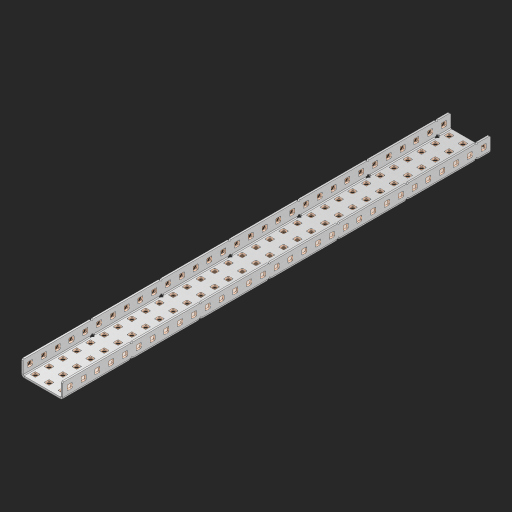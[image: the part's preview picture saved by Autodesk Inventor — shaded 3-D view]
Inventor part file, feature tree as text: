
AUTODESK INVENTOR PART (.ipt)
format: ipt  version: 2023 (Build 270158000, 158)  size: 1,850,368 bytes
history: native  units: in
note: dims shown in document units (in); Inventor stores cm internally (conversion verified against a paired STEP export)
features: other x160, extrude x154, sheet_metal_op x10, sketch x8, mirror x1, pattern_linear x1, chamfer x1
ambient origin geometry x8: Origin, YZ Plane, XZ Plane, XY Plane, X Axis, Y Axis, Z Axis, Center Point
bodies: Solid1 (feature_tree), Body (feature_tree)
feature tree (335):
  other  "Flange Pattern Plane"
  sheet_metal_op  "Flange Pattern"
  sheet_metal_op  "Body Pattern"
  other  "Arc Length"
  mirror  "Notch Mirror"
  pattern_linear  "Notch Pattern"  Spacing1=0.25in  [1 undecoded]
  chamfer  "End Chamfer"
  extrude  "Half Cut"  Depth=0.0625in
  sketch  "Sketch1"  dims[d0=1.5in]
  other  "Plate1"
  sketch  "Sketch2"  dims[d1=15.5in]
  other  "Plate2"
  sheet_metal_op  "Bend1"
  sheet_metal_op  "Corner1"
  sketch  "Sketch3"  dims[d2=0.0625in]
  other  "Flange Pattern Sketch"
  sketch  "Sketch7"  dims[d3=0.0625in]
  other  "Srf1"
  other  "Srf2"
  sketch  "Sketch8"  dims[d4=0.0312in]
  sketch  "Sketch9"  dims[d5=0.125in]
  other  "Srf91"
  sheet_metal_op  "Body Pattern Sketch"
  other  "Srf92"
  sketch  "Sketch13"  dims[d6=0.0625in]
  sketch  "Sketch14"  dims[d7=0.5in d8=90.0deg d9=0.0312in d10=0.25in d11=0.0625in d12=0.0625in d16=0.182in d17=0.02in d18=0.0625in d19=0.0in d20=0.25in d21=0.25in d46=0.172in d47=1.0in d48=0.0in d49=0.182in d50=0.02in d51=0.25in d52=0.25in d53=0.0625in d54=0.0in d55=0.172in d56=1.0in d57=0.0in d60=12.2047in d62=0.5in d63=1.1811in d65=0.5in d85=0.1473in d86=0.1782in d88=0.04in d89=0.0625in d90=0.0in d91=0.04in d92=0.0491in d95=2.5in d96=0.04in d97=0.25in d98=45.0deg d101=0.0in d102=2.497in d131=1.5in d132=12.2047in d134=0.5in d139=0.5in]
  other  "Srf856"
  other  "Srf1310"
  other  "Srf1311"
  other  "Srf1312"
  other  "Srf1376"
  other  "Srf1377"
  other  "Srf1728"
  other  "Srf1755"
  other  "Srf1878"
  other  "Srf1879"
  other  "Srf1880"
  other  "Srf1881"
  other  "Srf1882"
  other  "Srf1883"
  other  "Srf1884"
  other  "Srf1885"
  other  "Srf1886"
  other  "Srf1887"
  other  "Srf1888"
  other  "Srf1889"
  other  "Srf1890"
  other  "Srf1891"
  other  "Srf1892"
  other  "Srf1893"
  other  "Srf1894"
  other  "Srf1895"
  other  "Srf1896"
  other  "Srf1897"
  other  "Srf1898"
  other  "Srf1899"
  other  "Srf1900"
  other  "Srf1901"
  other  "Srf1902"
  other  "Srf1903"
  other  "Srf1904"
  other  "Srf1905"
  other  "Srf1906"
  other  "Srf1907"
  other  "Srf1908"
  other  "Srf1909"
  other  "Srf1910"
  other  "Srf1911"
  other  "Srf1912"
  other  "Srf1913"
  other  "Srf1914"
  other  "Srf1915"
  other  "Srf1916"
  other  "Srf1917"
  other  "Srf1918"
  other  "Srf1919"
  other  "Srf1920"
  other  "Srf1921"
  other  "Srf1922"
  other  "Srf1923"
  other  "Srf1924"
  other  "Srf1925"
  other  "Srf1926"
  other  "Srf1927"
  other  "Srf1928"
  other  "Srf1929"
  other  "Srf1930"
  other  "Srf1931"
  other  "Srf1932"
  other  "Srf1933"
  other  "Srf1942"
  other  "Srf1943"
  other  "Srf1944"
  other  "Srf1945"
  other  "Srf1946"
  other  "Srf1947"
  other  "Srf1948"
  other  "Srf1949"
  other  "Srf1950"
  other  "Srf1951"
  other  "Srf1952"
  other  "Srf1953"
  other  "Srf1954"
  other  "Srf1955"
  other  "Srf1956"
  other  "Srf1957"
  other  "Srf1958"
  other  "Srf1959"
  other  "Srf1960"
  other  "Srf1961"
  other  "Srf1962"
  other  "Srf1963"
  other  "Srf1964"
  other  "Srf1965"
  other  "Srf1966"
  other  "Srf1967"
  other  "Srf1968"
  other  "Srf1969"
  other  "Srf1970"
  other  "Srf1971"
  other  "Srf1972"
  other  "Srf1973"
  other  "Srf1974"
  other  "Srf1975"
  other  "Srf1976"
  other  "Srf1977"
  other  "Srf1978"
  other  "Srf1979"
  other  "Srf1980"
  other  "Srf1981"
  other  "Srf1982"
  other  "Srf1983"
  other  "Srf1984"
  other  "Srf1985"
  other  "Srf1986"
  other  "Srf1987"
  other  "Srf1988"
  other  "Srf1989"
  other  "Srf1990"
  other  "Srf1991"
  other  "Srf1992"
  other  "Srf1993"
  other  "Srf1994"
  other  "Srf1995"
  other  "Srf1996"
  other  "Srf1997"
  other  "Srf1998"
  other  "Srf1999"
  other  "Srf2000"
  other  "Srf2001"
  other  "Srf2002"
  other  "Srf2003"
  other  "Srf2004"
  other  "Srf2005"
  other  "Srf2006"
  other  "Srf2007"
  other  "Srf2008"
  other  "Srf2009"
  other  "Srf2010"
  other  "Srf2011"
  other  "Srf2012"
  other  "Srf2013"
  other  "Srf2014"
  other  "Srf2015"
  other  "Srf2016"
  other  "Srf2017"
  other  "Srf2018"
  other  "Srf2019"
  other  "Srf2020"
  other  "Srf2021"
  other  "Srf2022"
  other  "Srf2023"
  other  "Srf2024"
  other  "Srf2025"
  other  "Srf2026"
  other  "Srf2027"
  other  "Srf2028"
  sheet_metal_op  "Flange Stamp"
  sheet_metal_op  "Flange Circle"
  sheet_metal_op  "Body Stamp"
  sheet_metal_op  "Body Circle"
  sheet_metal_op  "Notch"
  extrude  "ExtrusionSrf2"  Depth=0.0625in
  extrude  "ExtrusionSrf92"  Depth=1.5in
  extrude  "ExtrusionSrf856"  Depth=0.02in
  extrude  "ExtrusionSrf1310"  Depth=0.0625in
  extrude  "ExtrusionSrf1311"  TaperAngle=0.0deg  [1 undecoded]
  extrude  "ExtrusionSrf1312"  Depth=0.25in
  extrude  "ExtrusionSrf1376"  Depth=0.25in
  extrude  "ExtrusionSrf1377"  Depth=1.5in
  extrude  "ExtrusionSrf1728"  Depth=1.5in TaperAngle=0.0deg
  extrude  "ExtrusionSrf1755"  Depth=1.5in
  extrude  "ExtrusionSrf1878"  Depth=0.02in
  extrude  "ExtrusionSrf1879"  Depth=0.25in
  extrude  "ExtrusionSrf1880"  Depth=0.25in
  extrude  "ExtrusionSrf1881"  Depth=0.0625in
  extrude  "ExtrusionSrf1882"  TaperAngle=0.0deg  [1 undecoded]
  extrude  "ExtrusionSrf1883"  Depth=1.5in
  extrude  "ExtrusionSrf1884"  Depth=1.5in TaperAngle=0.0deg
  extrude  "ExtrusionSrf1885"  Depth=1.5in
  extrude  "ExtrusionSrf1886"  Depth=1.5in
  extrude  "ExtrusionSrf1887"  Depth=1.5in
  extrude  "ExtrusionSrf1888"  Depth=1.5in
  extrude  "ExtrusionSrf1889"  Depth=1.5in
  extrude  "ExtrusionSrf1890"  Depth=0.0625in
  extrude  "ExtrusionSrf1891"  TaperAngle=0.0deg  [1 undecoded]
  extrude  "ExtrusionSrf1892"  Depth=1.5in
  extrude  "ExtrusionSrf1893"  Depth=1.5in
  extrude  "ExtrusionSrf1894"  Depth=1.5in
  extrude  "ExtrusionSrf1895"  Depth=0.25in TaperAngle=45.0deg
  extrude  "ExtrusionSrf1896"  TaperAngle=0.0deg  [1 undecoded]
  extrude  "ExtrusionSrf1897"  Depth=1.5in
  extrude  "ExtrusionSrf1898"  Depth=1.5in
  extrude  "ExtrusionSrf1899"  Depth=1.5in
  extrude  "ExtrusionSrf1900"  Depth=1.5in
  extrude  "ExtrusionSrf1901"  Depth=1.5in
  extrude  "ExtrusionSrf1902"  [1 undecoded]
  extrude  "ExtrusionSrf1903"  [1 undecoded]
  extrude  "ExtrusionSrf1904"  [1 undecoded]
  extrude  "ExtrusionSrf1905"  [1 undecoded]
  extrude  "ExtrusionSrf1906"  [1 undecoded]
  extrude  "ExtrusionSrf1907"  [1 undecoded]
  extrude  "ExtrusionSrf1908"  [1 undecoded]
  extrude  "ExtrusionSrf1909"  [1 undecoded]
  extrude  "ExtrusionSrf1910"  [1 undecoded]
  extrude  "ExtrusionSrf1911"  [1 undecoded]
  extrude  "ExtrusionSrf1912"  [1 undecoded]
  extrude  "ExtrusionSrf1913"  [1 undecoded]
  extrude  "ExtrusionSrf1914"  [1 undecoded]
  extrude  "ExtrusionSrf1915"  [1 undecoded]
  extrude  "ExtrusionSrf1916"  [1 undecoded]
  extrude  "ExtrusionSrf1917"  [1 undecoded]
  extrude  "ExtrusionSrf1918"  [1 undecoded]
  extrude  "ExtrusionSrf1919"  [1 undecoded]
  extrude  "ExtrusionSrf1920"  [1 undecoded]
  extrude  "ExtrusionSrf1921"  [1 undecoded]
  extrude  "ExtrusionSrf1922"  [1 undecoded]
  extrude  "ExtrusionSrf1923"  [1 undecoded]
  extrude  "ExtrusionSrf1924"  [1 undecoded]
  extrude  "ExtrusionSrf1925"  [1 undecoded]
  extrude  "ExtrusionSrf1926"  [1 undecoded]
  extrude  "ExtrusionSrf1927"  [1 undecoded]
  extrude  "ExtrusionSrf1928"  [1 undecoded]
  extrude  "ExtrusionSrf1929"  [1 undecoded]
  extrude  "ExtrusionSrf1930"  [1 undecoded]
  extrude  "ExtrusionSrf1931"  [1 undecoded]
  extrude  "ExtrusionSrf1932"  [1 undecoded]
  extrude  "ExtrusionSrf1933"  [1 undecoded]
  extrude  "ExtrusionSrf1942"  [1 undecoded]
  extrude  "ExtrusionSrf1943"  [1 undecoded]
  extrude  "ExtrusionSrf1944"  [1 undecoded]
  extrude  "ExtrusionSrf1945"  [1 undecoded]
  extrude  "ExtrusionSrf1946"  [1 undecoded]
  extrude  "ExtrusionSrf1947"  [1 undecoded]
  extrude  "ExtrusionSrf1948"  [1 undecoded]
  extrude  "ExtrusionSrf1949"  [1 undecoded]
  extrude  "ExtrusionSrf1950"  [1 undecoded]
  extrude  "ExtrusionSrf1951"  [1 undecoded]
  extrude  "ExtrusionSrf1952"  [1 undecoded]
  extrude  "ExtrusionSrf1953"  [1 undecoded]
  extrude  "ExtrusionSrf1954"  [1 undecoded]
  extrude  "ExtrusionSrf1955"  [1 undecoded]
  extrude  "ExtrusionSrf1956"  [1 undecoded]
  extrude  "ExtrusionSrf1957"  [1 undecoded]
  extrude  "ExtrusionSrf1958"  [1 undecoded]
  extrude  "ExtrusionSrf1959"  [1 undecoded]
  extrude  "ExtrusionSrf1960"  [1 undecoded]
  extrude  "ExtrusionSrf1961"  [1 undecoded]
  extrude  "ExtrusionSrf1962"  [1 undecoded]
  extrude  "ExtrusionSrf1963"  [1 undecoded]
  extrude  "ExtrusionSrf1964"  [1 undecoded]
  extrude  "ExtrusionSrf1965"  [1 undecoded]
  extrude  "ExtrusionSrf1966"  [1 undecoded]
  extrude  "ExtrusionSrf1967"  [1 undecoded]
  extrude  "ExtrusionSrf1968"  [1 undecoded]
  extrude  "ExtrusionSrf1969"  [1 undecoded]
  extrude  "ExtrusionSrf1970"  [1 undecoded]
  extrude  "ExtrusionSrf1971"  [1 undecoded]
  extrude  "ExtrusionSrf1972"  [1 undecoded]
  extrude  "ExtrusionSrf1973"  [1 undecoded]
  extrude  "ExtrusionSrf1974"  [1 undecoded]
  extrude  "ExtrusionSrf1975"  [1 undecoded]
  extrude  "ExtrusionSrf1976"  [1 undecoded]
  extrude  "ExtrusionSrf1977"  [1 undecoded]
  extrude  "ExtrusionSrf1978"  [1 undecoded]
  extrude  "ExtrusionSrf1979"  [1 undecoded]
  extrude  "ExtrusionSrf1980"  [1 undecoded]
  extrude  "ExtrusionSrf1981"  [1 undecoded]
  extrude  "ExtrusionSrf1982"  [1 undecoded]
  extrude  "ExtrusionSrf1983"  [1 undecoded]
  extrude  "ExtrusionSrf1984"  [1 undecoded]
  extrude  "ExtrusionSrf1985"  [1 undecoded]
  extrude  "ExtrusionSrf1986"  [1 undecoded]
  extrude  "ExtrusionSrf1987"  [1 undecoded]
  extrude  "ExtrusionSrf1988"  [1 undecoded]
  extrude  "ExtrusionSrf1989"  [1 undecoded]
  extrude  "ExtrusionSrf1990"  [1 undecoded]
  extrude  "ExtrusionSrf1991"  [1 undecoded]
  extrude  "ExtrusionSrf1992"  [1 undecoded]
  extrude  "ExtrusionSrf1993"  [1 undecoded]
  extrude  "ExtrusionSrf1994"  [1 undecoded]
  extrude  "ExtrusionSrf1995"  [1 undecoded]
  extrude  "ExtrusionSrf1996"  [1 undecoded]
  extrude  "ExtrusionSrf1997"  [1 undecoded]
  extrude  "ExtrusionSrf1998"  [1 undecoded]
  extrude  "ExtrusionSrf1999"  [1 undecoded]
  extrude  "ExtrusionSrf2000"  [1 undecoded]
  extrude  "ExtrusionSrf2001"  [1 undecoded]
  extrude  "ExtrusionSrf2002"  [1 undecoded]
  extrude  "ExtrusionSrf2003"  [1 undecoded]
  extrude  "ExtrusionSrf2004"  [1 undecoded]
  extrude  "ExtrusionSrf2005"  [1 undecoded]
  extrude  "ExtrusionSrf2006"  [1 undecoded]
  extrude  "ExtrusionSrf2007"  [1 undecoded]
  extrude  "ExtrusionSrf2008"  [1 undecoded]
  extrude  "ExtrusionSrf2009"  [1 undecoded]
  extrude  "ExtrusionSrf2010"  [1 undecoded]
  extrude  "ExtrusionSrf2011"  [1 undecoded]
  extrude  "ExtrusionSrf2012"  [1 undecoded]
  extrude  "ExtrusionSrf2013"  [1 undecoded]
  extrude  "ExtrusionSrf2014"  [1 undecoded]
  extrude  "ExtrusionSrf2015"  [1 undecoded]
  extrude  "ExtrusionSrf2016"  [1 undecoded]
  extrude  "ExtrusionSrf2017"  [1 undecoded]
  extrude  "ExtrusionSrf2018"  [1 undecoded]
  extrude  "ExtrusionSrf2019"  [1 undecoded]
  extrude  "ExtrusionSrf2020"  [1 undecoded]
  extrude  "ExtrusionSrf2021"  [1 undecoded]
  extrude  "ExtrusionSrf2022"  [1 undecoded]
  extrude  "ExtrusionSrf2023"  [1 undecoded]
  extrude  "ExtrusionSrf2024"  [1 undecoded]
  extrude  "ExtrusionSrf2025"  [1 undecoded]
  extrude  "ExtrusionSrf2026"  [1 undecoded]
  extrude  "ExtrusionSrf2027"  [1 undecoded]
  extrude  "ExtrusionSrf2028"  [1 undecoded]
note: 124 required parameter values undecoded (feature->parameter linkage not recoverable at this tier; creation-order binding heuristic only, values carry confidence <= 0.55)
